# Revit family: bimlib_narujnyeblokisistemakondicionirovaniya_mrv-s-ii_8-12hp_haier
name_source: partatom
category: Оборудование
units: mm (PartAtom-declared; Revit-internal decimal feet)

## family parameters
Всегда вертикально = Да
На основе рабочей плоскости = Нет
Общий = Нет
При загрузке вырезать с полостями = Нет
Размер круглого соединителя = Использовать диаметр
Тип детали = Нормальный
Точка расчета площади = Нет

## types (3) — shared parameters
ADSK_URL документации изделия = https://haierproff.ru
ADSK_URL страницы изделия = https://haierproff.ru
ADSK_Версия Revit = 2017
ADSK_Группирование = VRF-системы MRV-S''
ADSK_Единица измерения = шт.
ADSK_Завод-изготовитель = Haier Group
ADSK_Классификация нагрузок = ОВК
ADSK_Количество = 1
ADSK_Количество фаз = 3
ADSK_Коэффициент мощности = 1
ADSK_Масса = 149
ADSK_Напряжение = 400 В
ADSK_Обозначение = MRV-S'' серия AU
ADSK_Размер_Высота = 1636 мм
ADSK_Размер_Глубина = 400 мм
ADSK_Размер_Ширина = 1050 мм
ADSK_Расход воздуха = 10000.0 м³/ч
BL_BIM library = https://bimlib.pro
HG_URL поставщика = www.haierproff.ru
URL = www.haier.com
Заправка хладагента = 5.10 кг
Изготовитель = Haier Group
Производитель компрессора = MITSUBISHI ELECTRIC
Работа на обогрев = Нет
Рабочий диапазон_Обогрев = -20 ~ 27
Рабочий диапазон_Охлаждение = -5 ~ 48
Сбоку = Подключение : Сбоку
Сзади = Подключение : Сзади
Снизу = Подключение : Снизу
Спереди = Подключение : Спереди
Тип компрессора = Двухроторный
Тип хладагента = R410A
Частота тока = 50 Гц
zero-valued in all types: Отметка по умолчанию

## per-type parameters (varying)
| type | ADSK_Код изделия | ADSK_Наименование | ADSK_Наименование краткое | ADSK_Номинальная мощность | ADSK_Полная мощность | Диаметр_Газ | Диаметр_Жидкость | Звуковое давление_нагрев | Звуковое давление_охлаждение | Обогрев_Потребляемая мощность | Охлаждение_Потребляемая мощность | Теплопроизводительность | Холодопроизводительность |
| AU08NFKERA_8HP_HAIER | AU08NFKERA | Наружный блок VRF-системы кондиционирования MRV-S'',8HP | VRF-системы MRV-S'', 8HP | 6450 Вт | 6450 В·А | 19.05 мм | 9.52 мм | 65 | 63 | 6 кВт | 6 кВт | 23 кВт | 23 кВт |
| AU12NFKERA_12HP_HAIER | AU12NFKERA | Наружный блок VRF-системы кондиционирования MRV-S'',12HP | VRF-системы MRV-S'', 12HP | 11520 Вт | 11520 В·А | 25.4 мм | 12.7 мм | 67 | 65 | 8 кВт | 12 кВт | 32 кВт | 32 кВт |
| AU10NFKERA_10HP_HAIER | AU10NFKERA | Наружный блок VRF-системы кондиционирования MRV-S'',10HP | VRF-системы MRV-S'', 10HP | 8670 Вт | 8670 В·А | 22.22 мм | 9.52 мм | 66 | 64 | 8 кВт | 9 кВт | 31 кВт | 28 кВт |
